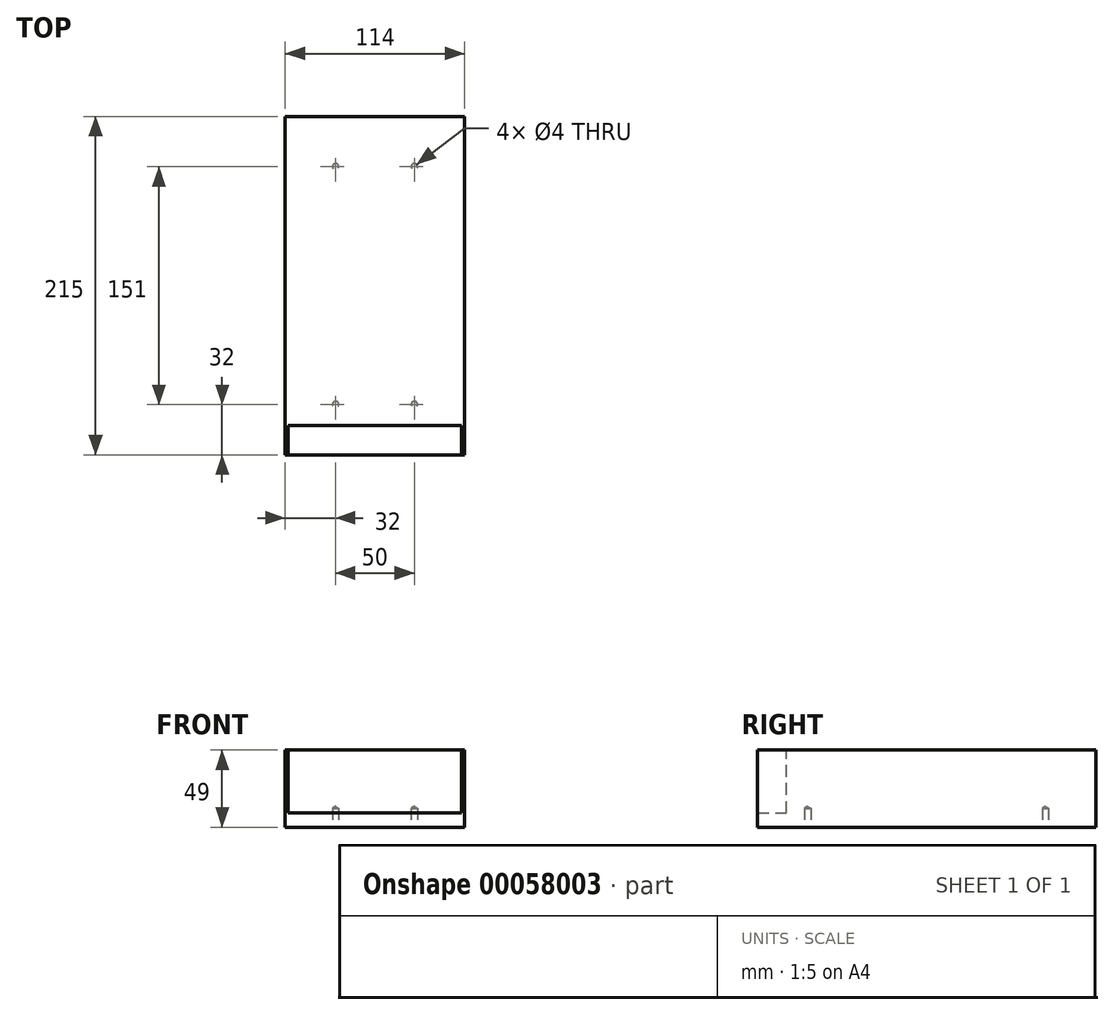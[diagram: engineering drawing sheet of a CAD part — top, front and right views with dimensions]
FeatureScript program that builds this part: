
annotation { "Feature Type Name" : "Feature", "Feature Type Description" : "" }
export const myFeature = defineFeature(function(context is Context, id is Id, definition is map)
    precondition{}
    {
        {
            var Q0;
            Q0=qCreatedBy(makeId("Right.planeOp"),FACE);
            var sketch = newSketch(context, id + "F0", { "sketchPlane" : qUnion([Q0])});
            skLineSegment(sketch, "E0", {"start": v(0, 0) * mm, "end": v(215, 0) * mm});
            skLineSegment(sketch, "E1", {"start": v(215, 0) * mm, "end": v(215, 49) * mm});
            skLineSegment(sketch, "E2", {"start": v(215, 49) * mm, "end": v(0, 49) * mm});
            skLineSegment(sketch, "E3", {"start": v(0, 49) * mm, "end": v(0, 0) * mm});
            skSolve(sketch);
        }
        {
            var Q0;
            Q0=makeQuery(id+"F0.imprint","IMPRINT",FACE,{"disambiguationData":[TD([[makeQuery(id+"F0.imprint","IMPRINT",EDGE,{"derivedFrom":sQuery(id+"F0.wireOp",EDGE,"E0")}),1.0]])]});
            extrude(context, id + "F1", {"entities" : qUnion([Q0]), "endBound" : BoundingType.SYMMETRIC, "depth" : 114 * mm});
        }
        {
            var Q0;
            Q0=makeQuery(id+"F1.opExtrude","SWEPT_FACE",FACE,{"disambiguationData":[OSD([sQuery(id+"F0.wireOp",EDGE,"E2")])]});
            var sketch = newSketch(context, id + "F2", { "sketchPlane" : qUnion([Q0])});
            skLineSegment(sketch, "E4.bottom", {"start": v(-55.1, 0) * mm, "end": v(55.1, 0) * mm});
            skLineSegment(sketch, "E4.top", {"start": v(-55.1, 18.5) * mm, "end": v(55.1, 18.5) * mm});
            skLineSegment(sketch, "E4.left", {"start": v(-55.1, 0) * mm, "end": v(-55.1, 18.5) * mm});
            skLineSegment(sketch, "E4.right", {"start": v(55.1, 0) * mm, "end": v(55.1, 18.5) * mm});
            skLineSegment(sketch, "E5", {"start": v(-55.1, 0) * mm, "end": v(-57, 0) * mm, "construction": true});
            skLineSegment(sketch, "E6", {"start": v(55.1, 0) * mm, "end": v(57, 0) * mm, "construction": true});
            skSolve(sketch);
        }
        {
            var Q0;
            Q0=makeQuery(id+"F2.imprint","IMPRINT",FACE,{"disambiguationData":[TD([[makeQuery(id+"F2.imprint","IMPRINT",EDGE,{"derivedFrom":sQuery(id+"F2.wireOp",EDGE,"E4.bottom")}),-1.0]])]});
            extrude(context, id + "F3", {"entities" : qUnion([Q0]), "operationType" : NewBodyOperationType.REMOVE, "oppositeDirection" : true, "depth" : 40 * mm});
        }
        {
            var Q0;
            Q0=makeQuery(id+"F1.opExtrude","SWEPT_FACE",FACE,{"disambiguationData":[OSD([sQuery(id+"F0.wireOp",EDGE,"E0")])]});
            var sketch = newSketch(context, id + "F4", { "sketchPlane" : qUnion([Q0])});
            skLineSegment(sketch, "E7.bottom", {"start": v(25, -32) * mm, "end": v(-25, -32) * mm, "construction": true});
            skLineSegment(sketch, "E7.top", {"start": v(25, -183) * mm, "end": v(-25, -183) * mm, "construction": true});
            skLineSegment(sketch, "E7.left", {"start": v(25, -32) * mm, "end": v(25, -183) * mm, "construction": true});
            skLineSegment(sketch, "E7.right", {"start": v(-25, -32) * mm, "end": v(-25, -183) * mm, "construction": true});
            skLineSegment(sketch, "E8", {"start": v(25, -32) * mm, "end": v(57, -32) * mm, "construction": true});
            skLineSegment(sketch, "E9", {"start": v(25, -32) * mm, "end": v(25, 0) * mm, "construction": true});
            skLineSegment(sketch, "E10", {"start": v(-25, -183) * mm, "end": v(-25, -215) * mm, "construction": true});
            skLineSegment(sketch, "E11", {"start": v(-25, -183) * mm, "end": v(-57, -183) * mm, "construction": true});
            skSolve(sketch);
        }
        {
            var Q0;
            Q0=sQuery(id+"F4.wireOp",VERTEX,"E7.left.start");
            var Q1;
            Q1=sQuery(id+"F4.wireOp",VERTEX,"E7.left.end");
            var Q2;
            Q2=sQuery(id+"F4.wireOp",VERTEX,"E7.top.end");
            var Q3;
            Q3=sQuery(id+"F4.wireOp",VERTEX,"E7.right.start");
            var Q4;
            Q4=makeQuery(id+"F1.opExtrude","SWEPT_BODY",BODY,{"disambiguationData":[OSD([sQuery(id+"F0.wireOp",EDGE,"E0"),sQuery(id+"F0.wireOp",EDGE,"E1"),sQuery(id+"F0.wireOp",EDGE,"E2"),sQuery(id+"F0.wireOp",EDGE,"E3")])]});
            hole(context, id + "F5", {"style" : HoleStyle.SIMPLE, "endStyle" : HoleEndStyle.BLIND, "holeDiameter" : 4 * mm, "holeDepth" : 12 * mm, "locations" : qUnion([Q0, Q1, Q2, Q3]), "scope" : qUnion([Q4])});
        }
    });
